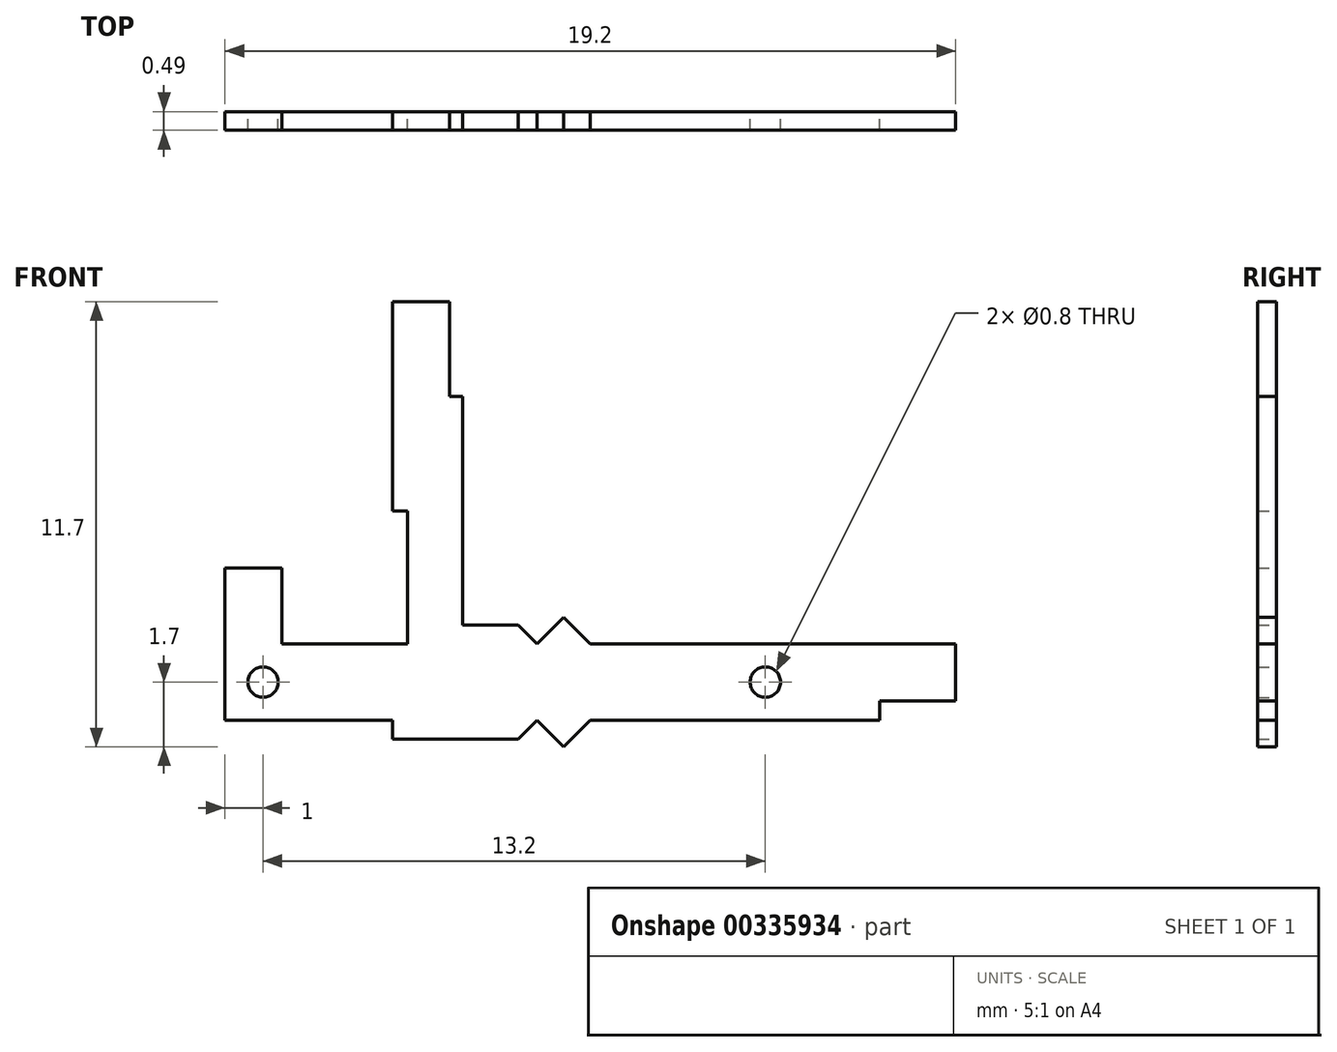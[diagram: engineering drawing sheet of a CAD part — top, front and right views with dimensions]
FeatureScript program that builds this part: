
annotation { "Feature Type Name" : "Feature", "Feature Type Description" : "" }
export const myFeature = defineFeature(function(context is Context, id is Id, definition is map)
    precondition{}
    {
        {
            var Q0;
            Q0=qCreatedBy(makeId("Front.planeOp"),FACE);
            var sketch = newSketch(context, id + "F0", { "sketchPlane" : qUnion([Q0])});
            skLineSegment(sketch, "E0", {"start": v(-1, 3) * mm, "end": v(-1, -1) * mm});
            skLineSegment(sketch, "E1", {"start": v(-1, -1) * mm, "end": v(3.4, -1) * mm});
            skLineSegment(sketch, "E2", {"start": v(3.4, -1) * mm, "end": v(3.4, -1.5) * mm});
            skLineSegment(sketch, "E3", {"start": v(3.4, -1.5) * mm, "end": v(6.7, -1.5) * mm});
            skLineSegment(sketch, "E4", {"start": v(6.7, -1.5) * mm, "end": v(7.2, -1) * mm});
            skLineSegment(sketch, "E5", {"start": v(7.2, -1) * mm, "end": v(7.9, -1.7) * mm});
            skLineSegment(sketch, "E6", {"start": v(7.9, -1.7) * mm, "end": v(8.6, -1) * mm});
            skLineSegment(sketch, "E7", {"start": v(8.6, -1) * mm, "end": v(16.2, -1) * mm});
            skLineSegment(sketch, "E8", {"start": v(16.2, -1) * mm, "end": v(16.2, -0.5) * mm});
            skLineSegment(sketch, "E9", {"start": v(16.2, -0.5) * mm, "end": v(18.2, -0.5) * mm});
            skLineSegment(sketch, "E10", {"start": v(18.2, -0.5) * mm, "end": v(18.2, 1) * mm});
            skLineSegment(sketch, "E11", {"start": v(18.2, 1) * mm, "end": v(8.6, 1) * mm});
            skLineSegment(sketch, "E12", {"start": v(8.6, 1) * mm, "end": v(7.9, 1.7) * mm});
            skLineSegment(sketch, "E13", {"start": v(7.9, 1.7) * mm, "end": v(7.2, 1) * mm});
            skLineSegment(sketch, "E14", {"start": v(7.2, 1) * mm, "end": v(6.7, 1.5) * mm});
            skLineSegment(sketch, "E15", {"start": v(6.7, 1.5) * mm, "end": v(5.25, 1.5) * mm});
            skLineSegment(sketch, "E16", {"start": v(5.25, 1.5) * mm, "end": v(5.25, 7.5) * mm});
            skLineSegment(sketch, "E17", {"start": v(5.25, 7.5) * mm, "end": v(4.9, 7.5) * mm});
            skLineSegment(sketch, "E18", {"start": v(4.9, 7.5) * mm, "end": v(4.9, 10) * mm});
            skLineSegment(sketch, "E19", {"start": v(4.9, 10) * mm, "end": v(3.4, 10) * mm});
            skLineSegment(sketch, "E20", {"start": v(3.4, 10) * mm, "end": v(3.4, 4.5) * mm});
            skLineSegment(sketch, "E21", {"start": v(3.4, 4.5) * mm, "end": v(3.8, 4.5) * mm});
            skLineSegment(sketch, "E22", {"start": v(3.8, 4.5) * mm, "end": v(3.8, 1) * mm});
            skLineSegment(sketch, "E23", {"start": v(3.8, 1) * mm, "end": v(0.5, 1) * mm});
            skLineSegment(sketch, "E24", {"start": v(0.5, 1) * mm, "end": v(0.5, 3) * mm});
            skLineSegment(sketch, "E25", {"start": v(0.5, 3) * mm, "end": v(-1, 3) * mm});
            skCircle(sketch, "E26", {"center": v(0, 0) * mm, "radius": 0.4 * mm});
            skCircle(sketch, "E27", {"center": v(13.2, 0) * mm, "radius": 0.4 * mm});
            skSolve(sketch);
        }
        {
            var Q0;
            Q0 = qSketchRegion(id + "F0", true);
            extrude(context, id + "F1", {"entities" : qUnion([Q0]), "depth" : 0.49 * mm});
        }
    });
